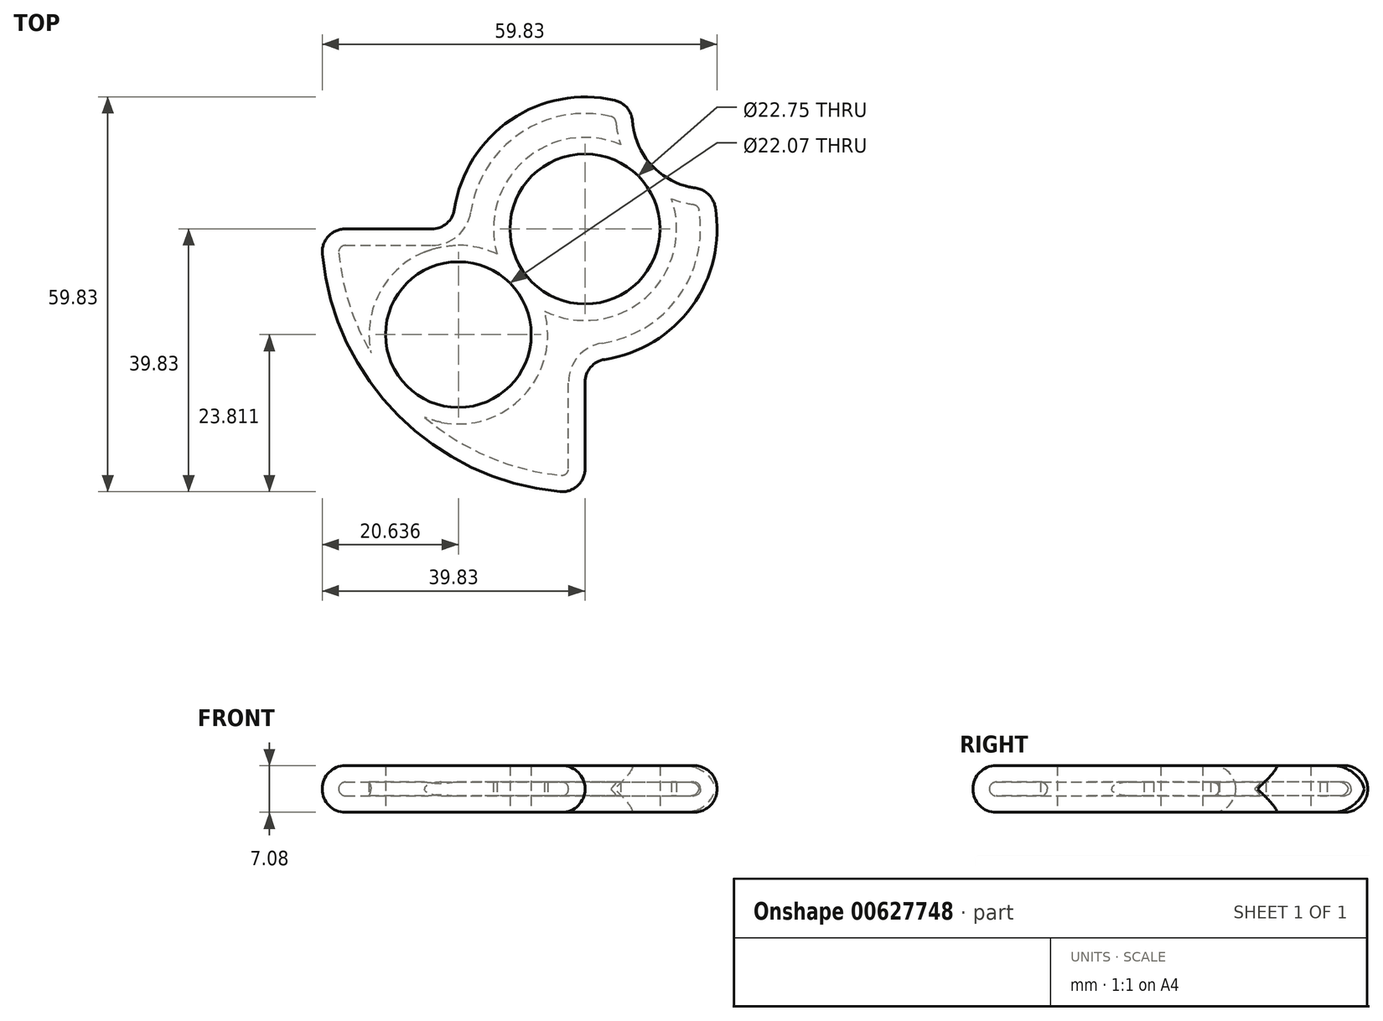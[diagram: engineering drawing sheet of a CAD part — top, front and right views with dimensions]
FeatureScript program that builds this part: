
annotation { "Feature Type Name" : "Feature", "Feature Type Description" : "" }
export const myFeature = defineFeature(function(context is Context, id is Id, definition is map)
    precondition{}
    {
        {
            var Q0;
            Q0=qCreatedBy(makeId("Top.planeOp"),FACE);
            var sketch = newSketch(context, id + "F0", { "sketchPlane" : qUnion([Q0])});
            skArc(sketch, "E0", {"start": v(0, 40) * mm, "mid": v(28.28, 28.28) * mm, "end": v(40, 0) * mm});
            skArc(sketch, "E1", {"start": v(-40, 0) * mm, "mid": v(-28.28, -28.28) * mm, "end": v(0, -40) * mm});
            skLineSegment(sketch, "E2", {"start": v(-40, 0) * mm, "end": v(0, 0) * mm});
            skLineSegment(sketch, "E3", {"start": v(0, 0) * mm, "end": v(0, 40) * mm});
            skLineSegment(sketch, "E4", {"start": v(0, 0) * mm, "end": v(40, 0) * mm});
            skLineSegment(sketch, "E5", {"start": v(0, 0) * mm, "end": v(0, -40) * mm});
            skCircle(sketch, "E6", {"center": v(0, 0) * mm, "radius": 20 * mm});
            skPoint(sketch, "E7", {"position": v(-19.2, -16.02) * mm});
            skPoint(sketch, "E8", {"position": v(18.2, 17.14) * mm});
            skSolve(sketch);
        }
        {
            var Q0;
            {var subQ0=sQuery(id+"F0.wireOp",EDGE,"E1");Q0=makeQuery(id+"F0.imprint","IMPRINT",FACE,{"disambiguationData":[TD([[makeQuery(id+"F0.imprint","IMPRINT",EDGE,{"derivedFrom":subQ0}),1.0]])]});}
            var Q1;
            {var subQ0=sQuery(id+"F0.wireOp",EDGE,"E0");Q1=makeQuery(id+"F0.imprint","IMPRINT",FACE,{"disambiguationData":[TD([[makeQuery(id+"F0.imprint","IMPRINT",EDGE,{"derivedFrom":subQ0}),-1.0]])]});}
            var Q2;
            {var subQ1=sQuery(id+"F0.wireOp",EDGE,"E2");var subQ3=sQuery(id+"F0.wireOp",EDGE,"E6");var subQ4=makeQuery(id+"F0.imprint","INTERSECT",VERTEX,{"derivedFrom":[subQ1,subQ3]});Q2=makeQuery(id+"F0.imprint","IMPRINT",FACE,{"disambiguationData":[TD([[makeQuery(id+"F0.imprint","IMPRINT",EDGE,{"disambiguationData":[TD([[subQ4,1.0]])],"derivedFrom":subQ3}),1.0]])]});}
            var Q3;
            {var subQ1=sQuery(id+"F0.wireOp",EDGE,"E4");var subQ3=sQuery(id+"F0.wireOp",EDGE,"E6");var subQ4=makeQuery(id+"F0.imprint","INTERSECT",VERTEX,{"derivedFrom":[subQ1,subQ3]});Q3=makeQuery(id+"F0.imprint","IMPRINT",FACE,{"disambiguationData":[TD([[makeQuery(id+"F0.imprint","IMPRINT",EDGE,{"disambiguationData":[TD([[subQ4,1.0]])],"derivedFrom":subQ3}),1.0]])]});}
            var Q4;
            {var subQ1=sQuery(id+"F0.wireOp",EDGE,"E3");var subQ3=sQuery(id+"F0.wireOp",EDGE,"E6");var subQ4=makeQuery(id+"F0.imprint","INTERSECT",VERTEX,{"derivedFrom":[subQ1,subQ3]});Q4=makeQuery(id+"F0.imprint","IMPRINT",FACE,{"disambiguationData":[TD([[makeQuery(id+"F0.imprint","IMPRINT",EDGE,{"disambiguationData":[TD([[subQ4,1.0]])],"derivedFrom":subQ3}),1.0]])]});}
            var Q5;
            {var subQ1=sQuery(id+"F0.wireOp",EDGE,"E2");var subQ3=sQuery(id+"F0.wireOp",EDGE,"E6");var subQ4=makeQuery(id+"F0.imprint","INTERSECT",VERTEX,{"derivedFrom":[subQ1,subQ3]});Q5=makeQuery(id+"F0.imprint","IMPRINT",FACE,{"disambiguationData":[TD([[makeQuery(id+"F0.imprint","IMPRINT",EDGE,{"disambiguationData":[TD([[subQ4,-1.0]])],"derivedFrom":subQ3}),1.0]])]});}
            extrude(context, id + "F1", {"entities" : qUnion([Q0, Q1, Q2, Q3, Q4, Q5]), "depth" : 7.08 * mm, "offsetDistance" : 25 * mm});
        }
        {
            var Q0;
            Q0=sQuery(id+"F0.wireOp",VERTEX,"E0.center");
            var Q1;
            Q1=makeQuery(id+"F1.opExtrude","SWEPT_BODY",BODY,{"disambiguationData":[OSD([sQuery(id+"F0.wireOp",EDGE,"E0"),sQuery(id+"F0.wireOp",EDGE,"E1"),sQuery(id+"F0.wireOp",EDGE,"E2"),sQuery(id+"F0.wireOp",EDGE,"E3"),sQuery(id+"F0.wireOp",EDGE,"E4"),sQuery(id+"F0.wireOp",EDGE,"E5"),sQuery(id+"F0.wireOp",EDGE,"E6")])]});
            hole(context, id + "F2", {"style" : HoleStyle.SIMPLE, "endStyle" : HoleEndStyle.BLIND, "oppositeDirection" : true, "holeDiameter" : 22.75 * mm, "majorDiameter" : 5 * mm, "holeDepth" : 12 * mm, "isTappedThrough" : true, "tappedDepth" : 12 * mm, "tapClearance" : 3, "locations" : qUnion([Q0]), "scope" : qUnion([Q1])});
        }
        {
            var Q0;
            Q0=sQuery(id+"F0.wireOp",VERTEX,"E7");
            var Q1;
            Q1=sQuery(id+"F0.wireOp",VERTEX,"E8");
            var Q2;
            Q2=makeQuery(id+"F1.opExtrude","SWEPT_BODY",BODY,{"disambiguationData":[OSD([sQuery(id+"F0.wireOp",EDGE,"E0"),sQuery(id+"F0.wireOp",EDGE,"E1"),sQuery(id+"F0.wireOp",EDGE,"E2"),sQuery(id+"F0.wireOp",EDGE,"E3"),sQuery(id+"F0.wireOp",EDGE,"E4"),sQuery(id+"F0.wireOp",EDGE,"E5"),sQuery(id+"F0.wireOp",EDGE,"E6")])]});
            hole(context, id + "F3", {"style" : HoleStyle.SIMPLE, "endStyle" : HoleEndStyle.BLIND, "oppositeDirection" : true, "holeDiameter" : 22.07 * mm, "majorDiameter" : 5 * mm, "holeDepth" : 35.38 * mm, "isTappedThrough" : true, "tappedDepth" : 12 * mm, "tapClearance" : 3, "locations" : qUnion([Q0, Q1]), "scope" : qUnion([Q2])});
        }
        {
            var Q0;
            Q0=makeQuery(id+"F1.opExtrude","SWEPT_FACE",FACE,{"disambiguationData":[OSD([sQuery(id+"F0.wireOp",EDGE,"E0")])]});
            var Q1;
            Q1=makeQuery(id+"F1.opExtrude","SWEPT_FACE",FACE,{"disambiguationData":[OSD([sQuery(id+"F0.wireOp",EDGE,"E2")])]});
            var Q2;
            {var subQ0=sQuery(id+"F0.wireOp",EDGE,"E6");Q2=makeQuery(id+"F1.opExtrude","SWEPT_FACE",FACE,{"disambiguationData":[OSD([subQ0]),TDD([makeQuery(id+"F0.imprint","IMPRINT",EDGE,{"disambiguationData":[TD([[makeQuery(id+"F0.imprint","INTERSECT",VERTEX,{"derivedFrom":[sQuery(id+"F0.wireOp",EDGE,"E2"),subQ0]}),1.0]])],"derivedFrom":subQ0})])]});}
            var Q3;
            Q3=makeQuery(id+"F1.opExtrude","SWEPT_FACE",FACE,{"disambiguationData":[OSD([sQuery(id+"F0.wireOp",EDGE,"E1")])]});
            var Q4;
            {var subQ0=sQuery(id+"F0.wireOp",EDGE,"E6");Q4=makeQuery(id+"F1.opExtrude","SWEPT_FACE",FACE,{"disambiguationData":[OSD([subQ0]),TDD([makeQuery(id+"F0.imprint","IMPRINT",EDGE,{"disambiguationData":[TD([[makeQuery(id+"F0.imprint","INTERSECT",VERTEX,{"derivedFrom":[sQuery(id+"F0.wireOp",EDGE,"E4"),subQ0]}),1.0]])],"derivedFrom":subQ0})])]});}
            var Q5;
            Q5=makeQuery(id+"F1.opExtrude","SWEPT_FACE",FACE,{"disambiguationData":[OSD([sQuery(id+"F0.wireOp",EDGE,"E4")])]});
            var Q6;
            Q6=makeQuery(id+"F1.opExtrude","SWEPT_FACE",FACE,{"disambiguationData":[OSD([sQuery(id+"F0.wireOp",EDGE,"E5")])]});
            var Q7;
            Q7=makeQuery(id+"F1.opExtrude","SWEPT_FACE",FACE,{"disambiguationData":[OSD([sQuery(id+"F0.wireOp",EDGE,"E3")])]});
            fillet(context, id + "F4", {"entities" : qUnion([Q0, Q1, Q2, Q3, Q4, Q5, Q6, Q7]), "radius" : 3.5 * mm, "tangentPropagation" : true, "allowEdgeOverflow" : false});
        }
        {
            var Q0;
            Q0=makeQuery(id+"F1.opExtrude","CAP_FACE",FACE,{"disambiguationData":[OSD([sQuery(id+"F0.wireOp",EDGE,"E0"),sQuery(id+"F0.wireOp",EDGE,"E1"),sQuery(id+"F0.wireOp",EDGE,"E2"),sQuery(id+"F0.wireOp",EDGE,"E3"),sQuery(id+"F0.wireOp",EDGE,"E4"),sQuery(id+"F0.wireOp",EDGE,"E5"),sQuery(id+"F0.wireOp",EDGE,"E6")])],"isStart":false});
            var Q1;
            Q1=makeQuery(id+"F1.opExtrude","SWEPT_BODY",BODY,{"disambiguationData":[OSD([sQuery(id+"F0.wireOp",EDGE,"E0"),sQuery(id+"F0.wireOp",EDGE,"E1"),sQuery(id+"F0.wireOp",EDGE,"E2"),sQuery(id+"F0.wireOp",EDGE,"E3"),sQuery(id+"F0.wireOp",EDGE,"E4"),sQuery(id+"F0.wireOp",EDGE,"E5"),sQuery(id+"F0.wireOp",EDGE,"E6")])]});
            shell(context, id + "F5", {"isHollow" : true, "entities" : qUnion([Q0]), "parts" : qUnion([Q1]), "thickness" : 2.5 * mm});
        }
    });
